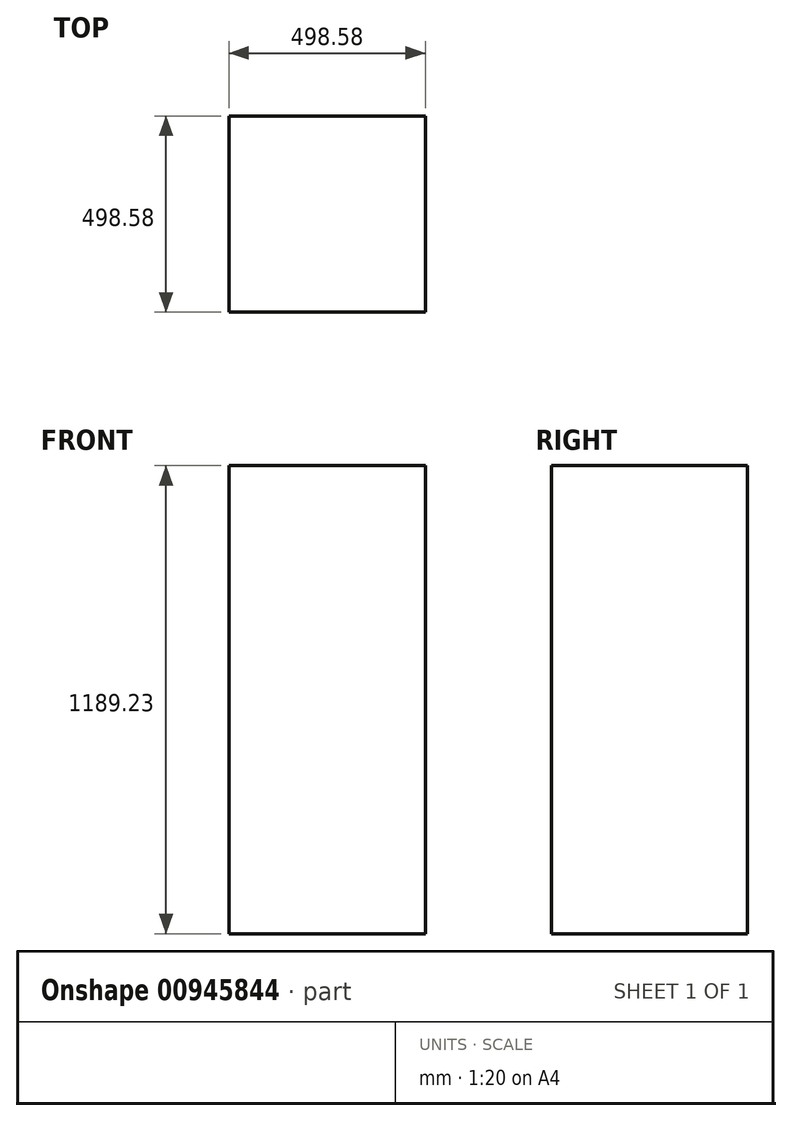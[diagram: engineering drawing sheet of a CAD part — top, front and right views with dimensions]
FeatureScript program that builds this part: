
annotation { "Feature Type Name" : "Feature", "Feature Type Description" : "" }
export const myFeature = defineFeature(function(context is Context, id is Id, definition is map)
    precondition{}
    {
        {
            var Q0;
            Q0=qCreatedBy(makeId("Top.planeOp"),FACE);
            var sketch = newSketch(context, id + "F0", { "sketchPlane" : qUnion([Q0])});
            skLineSegment(sketch, "E0.bottom", {"start": v(-498.58, 498.58) * mm, "end": v(0, 498.58) * mm});
            skLineSegment(sketch, "E0.top", {"start": v(-498.58, 0) * mm, "end": v(0, 0) * mm});
            skLineSegment(sketch, "E0.left", {"start": v(-498.58, 498.58) * mm, "end": v(-498.58, 0) * mm});
            skLineSegment(sketch, "E0.right", {"start": v(0, 498.58) * mm, "end": v(0, 0) * mm});
            skSolve(sketch);
        }
        {
            var Q0;
            Q0=makeQuery(id+"F0.imprint","IMPRINT",FACE,{"disambiguationData":[TD([[makeQuery(id+"F0.imprint","IMPRINT",EDGE,{"derivedFrom":sQuery(id+"F0.wireOp",EDGE,"E0.bottom")}),-1.0]])]});
            extrude(context, id + "F1", {"entities" : qUnion([Q0]), "depth" : 1189.23 * mm, "offsetDistance" : 25.4 * mm});
        }
    });
